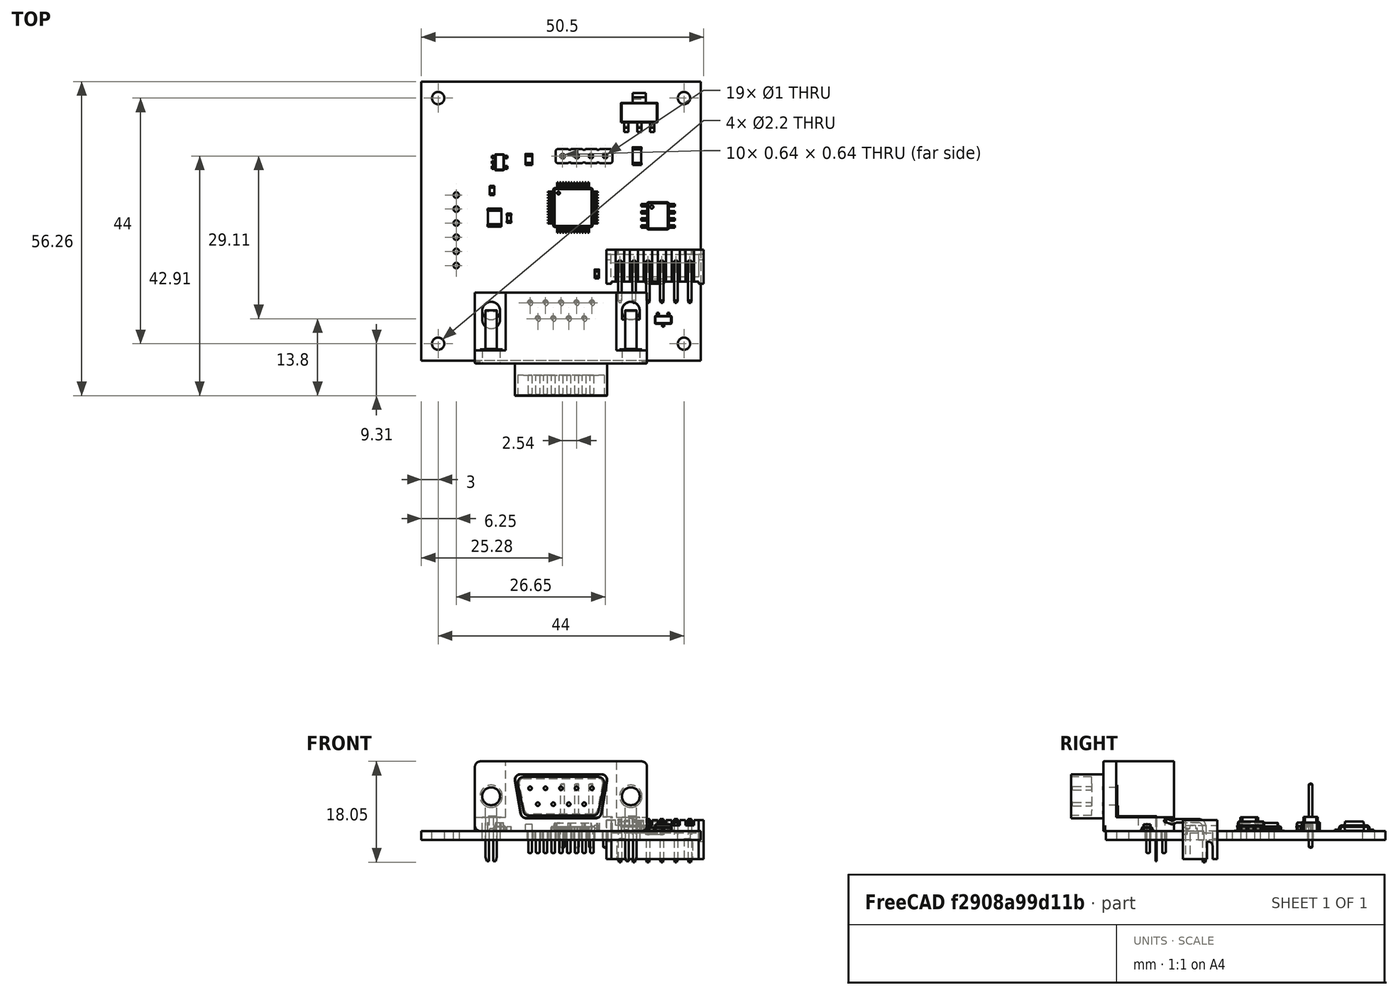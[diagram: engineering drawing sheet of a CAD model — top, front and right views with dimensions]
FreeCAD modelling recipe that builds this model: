
FCSTD DOCUMENT  (FreeCAD 0.21R33694 (Git))
Label: CTB-02_Assembled
License: All rights reserved
LicenseURL: http://en.wikipedia.org/wiki/All_rights_reserved
objects: App::Link×39, Part::Feature×34, App::Part×7, PartDesign::CoordinateSystem×1, Sketcher::SketchObject×1
note: 36 computed .brp shape members not serialized (recipe doc carries the construction recipe); baked Part::Feature solids carry a one-line shape summary decoded from their .brp

FEATURE [PartDesign::CoordinateSystem] Local_CS_1da8
  AttacherType = Attacher::AttachEngine3D
  MapMode = 2
  Support = -> [X_Axis001]
FEATURE [Part::Feature] Pcb_1da8
  Placement = pos=(-166.8,101.25,0) rot=(0,0,1;0rad)
  shape: bbox 50 x 50 x 1.6 mm, 31 faces (baked)
FEATURE [Sketcher::SketchObject] PCB_Sketch_1da8
  FullyConstrained = false
  sketch-geometry (4):
    g0: LineSegment StartX=-41.8 StartY=36.205 StartZ=0 EndX=8.2 EndY=36.205 EndZ=0
    g1: LineSegment StartX=8.2 StartY=36.205 StartZ=0 EndX=8.2 EndY=-13.795 EndZ=0
    g2: LineSegment StartX=8.2 StartY=-13.795 StartZ=0 EndX=-41.8 EndY=-13.795 EndZ=0
    g3: LineSegment StartX=-41.8 StartY=-13.795 StartZ=0 EndX=-41.8 EndY=36.205 EndZ=0
  constraints (4):
    c: Coincident(g2,g3)
    c: Coincident(g0,g3)
    c: Coincident(g1,g2)
    c: Coincident(g0,g1)
FEATURE [Part::Feature] Shape  label="R20_R_0603_1608Metric_5fb996311727"
  Placement = pos=(-29.15,16.7,0) rot=(0,0,1;1.5708rad)
  shape: bbox 0.8 x 1.6 x 0.45 mm, 26 faces (baked)
FEATURE [App::Link] R20_R_0603_1608Metric_5fb996311727_ln_  label="R8_R_0603_1608Metric_f8a9e1f5329c"
  LinkPlacement = pos=(1.6,-1.95,0) rot=(0,0,1;3.14159rad)
  LinkedObject = -> Shape
  Placement = pos=(1.6,-1.95,0) rot=(0,0,1;3.14159rad)
FEATURE [App::Link] R20_R_0603_1608Metric_5fb996311727_ln_001  label="R15_R_0603_1608Metric_9044ff0b4708"
  LinkPlacement = pos=(2.24952,17.675,0) rot=(0,0,-1;1.5708rad)
  LinkedObject = -> Shape
  Placement = pos=(2.24952,17.675,0) rot=(0,0,-1;1.5708rad)
FEATURE [App::Link] R20_R_0603_1608Metric_5fb996311727_ln_002  label="R2_R_0603_1608Metric_8a343aae5cf4"
  LinkPlacement = pos=(-31.05,26.5,0) rot=(0,0,-1;1.5708rad)
  LinkedObject = -> Shape
  Placement = pos=(-31.05,26.5,0) rot=(0,0,-1;1.5708rad)
FEATURE [App::Link] R20_R_0603_1608Metric_5fb996311727_ln_003  label="R14_R_0603_1608Metric_1eee93c9d580"
  LinkPlacement = pos=(4.24952,17.65,0) rot=(0,0,-1;1.5708rad)
  LinkedObject = -> Shape
  Placement = pos=(4.24952,17.65,0) rot=(0,0,-1;1.5708rad)
FEATURE [App::Link] R20_R_0603_1608Metric_5fb996311727_ln_004  label="R24_R_0603_1608Metric_4744c90dbd69"
  LinkPlacement = pos=(-28.8,6.7,0) rot=(0,0,1;0rad)
  LinkedObject = -> Shape
  Placement = pos=(-28.8,6.7,0) rot=(0,0,1;0rad)
FEATURE [App::Link] R20_R_0603_1608Metric_5fb996311727_ln_005  label="R9_R_0603_1608Metric_2fc7657f437f"
  LinkPlacement = pos=(-31.75,24.1,0) rot=(0,0,1;0rad)
  LinkedObject = -> Shape
  Placement = pos=(-31.75,24.1,0) rot=(0,0,1;0rad)
FEATURE [App::Link] R20_R_0603_1608Metric_5fb996311727_ln_006  label="R4_R_0603_1608Metric_9dc4eea49bad"
  LinkPlacement = pos=(-32.8,21.75,0) rot=(0,0,1;1.5708rad)
  LinkedObject = -> Shape
  Placement = pos=(-32.8,21.75,0) rot=(0,0,1;1.5708rad)
FEATURE [Part::Feature] Part__Feature  label="pin^SxB-XH-A-1(LF)(SN)_bent"
  shape: bbox 0.64 x 7.495 x 7.72 mm, 44 faces (baked)
FEATURE [Part::Feature] Part__Feature001  label="pin^SxB-XH-A-1(LF)(SN)"
  Placement = pos=(-2.5,2e-16,0) rot=(0,0,1;0rad)
  shape: bbox 0.64 x 7.495 x 7.72 mm, 22 faces (baked)
FEATURE [Part::Feature] Part__Feature002  label="pin^SxB-XH-A-1(LF)(SN)001"
  Placement = pos=(-5,5e-16,-1e-16) rot=(0,0,1;0rad)
  shape: bbox 0.64 x 7.495 x 7.72 mm, 22 faces (baked)
FEATURE [Part::Feature] Part__Feature003  label="pin^SxB-XH-A-1(LF)(SN)002"
  Placement = pos=(-7.5,7e-16,-1e-16) rot=(0,0,1;0rad)
  shape: bbox 0.64 x 7.495 x 7.72 mm, 22 faces (baked)
FEATURE [Part::Feature] Part__Feature004  label="pin^SxB-XH-A-1(LF)(SN)003"
  Placement = pos=(-10,1e-15,-1e-16) rot=(0,0,1;0rad)
  shape: bbox 0.64 x 7.495 x 7.72 mm, 22 faces (baked)
FEATURE [Part::Feature] Part__Feature005  label="pin^SxB-XH-A-1(LF)(SN)_bent001"
  Placement = pos=(-12.5,1.2e-15,-2e-16) rot=(0,0,1;0rad)
  shape: bbox 0.64 x 7.495 x 7.72 mm, 44 faces (baked)
FEATURE [Part::Feature] Part__Feature006  label="Body"
  Placement = pos=(6e-16,0,-5) rot=(0,1,0;3.14159rad)
  shape: bbox 17.4 x 6.1 x 7 mm, 94 faces (baked)
FEATURE [App::Part] S6B_XH_A_1  label="J2_S6B-XH-A-1_9f07903cdd4e"
  Group = -> [Part__Feature,Part__Feature001,Part__Feature002,Part__Feature003,Part__Feature004,Part__Feature005,Part__Feature006]
  Origin = -> Origin008
  Placement = pos=(-37.4,9.585,0) rot=(0.57735,0.57735,0.57735;2.0944rad)
FEATURE [App::Link] R20_R_0603_1608Metric_5fb996311727_ln_007  label="R30_R_0603_1608Metric_28c4134f9de7"
  LinkPlacement = pos=(-8.35,7.15,0) rot=(0,0,1;1.5708rad)
  LinkedObject = -> Shape
  Placement = pos=(-8.35,7.15,0) rot=(0,0,1;1.5708rad)
FEATURE [Part::Feature] Shape001  label="U3_SOT_223_728849c4b83c"
  Placement = pos=(-2.8,30.65,0) rot=(0,0,1;1.5708rad)
  shape: bbox 6.5 x 7 x 1.7 mm, 78 faces (baked)
FEATURE [App::Link] R20_R_0603_1608Metric_5fb996311727_ln_008  label="R12_R_0603_1608Metric_dfdb8e1241b6"
  LinkPlacement = pos=(-20.55,22,0) rot=(0,0,-1;1.5708rad)
  LinkedObject = -> Shape
  Placement = pos=(-20.55,22,0) rot=(0,0,-1;1.5708rad)
FEATURE [Part::Feature] Shape002  label="Q1_SOT_23_b1036018b4d2"
  Placement = pos=(1.5,-6.45,0) rot=(0,0,-1;1.5708rad)
  shape: bbox 3 x 2.5 x 1.2 mm, 76 faces (baked)
FEATURE [Part::Feature] Part__Feature007  label="CSTNE8M00GH5C000R0"
  shape: bbox 3 x 0.3 x 1.1 mm, 18 faces (baked)
FEATURE [Part::Feature] Part__Feature008  label="CSTNE8M00GH5C000R001"
  shape: bbox 0.2 x 0.5 x 1.3 mm, 6 faces (baked)
FEATURE [Part::Feature] Part__Feature009  label="CSTNE8M00GH5C000R002"
  shape: bbox 0.2 x 0.5 x 1.3 mm, 6 faces (baked)
FEATURE [Part::Feature] Part__Feature010  label="CSTNE8M00GH5C000R003"
  shape: bbox 0.4 x 0.5 x 1.3 mm, 6 faces (baked)
FEATURE [Part::Feature] Part__Feature011  label="CSTNE8M00GH5C000R004"
  shape: bbox 0.4 x 0.5 x 1.3 mm, 6 faces (baked)
FEATURE [Part::Feature] Part__Feature012  label="CSTNE8M00GH5C000R005"
  shape: bbox 0.4 x 0.45 x 1.3 mm, 6 faces (baked)
FEATURE [Part::Feature] Part__Feature013  label="CSTNE8M00GH5C000R006"
  shape: bbox 2 x 0.5 x 1.3 mm, 10 faces (baked)
FEATURE [App::Part] CSTNE8M00GH5C000R0  label="Y1_CSTNE8M00GH5C000R007_5459dfa8324f"
  Group = -> [Part__Feature007,Part__Feature008,Part__Feature009,Part__Feature010,Part__Feature011,Part__Feature012,Part__Feature013]
  Origin = -> Origin009
  Placement = pos=(-21.5,13.15,0) rot=(0.57735,-0.57735,-0.57735;2.0944rad)
FEATURE [Part::Feature] Shape003  label="C9_C_1206_3216Metric_4a6abfde341f"
  Placement = pos=(-3.2,22.85,0) rot=(0,0,1;1.5708rad)
  shape: bbox 1.6 x 3.2 x 1.6 mm, 28 faces (baked)
FEATURE [Part::Feature] Shape004  label="C13_C_0603_1608Metric_ec762f584ad8"
  Placement = pos=(-26.1,11.75,0) rot=(0,0,1;1.5708rad)
  shape: bbox 0.8 x 1.6 x 0.8 mm, 28 faces (baked)
FEATURE [Part::Feature] Shape005  label="D2_LED_0603_1608Metric_9a2b872fa988"
  Placement = pos=(-10.4,1.75,0) rot=(0,0,1;1.5708rad)
  shape: bbox 0.8 x 1.6 x 1.1 mm, 50 faces (baked)
FEATURE [App::Link] U3_SOT_223_728849c4b83c_ln_  label="U1_SOT_223_b2e5ecc5a7cd"
  LinkPlacement = pos=(-21.5,30.65,0) rot=(0,0,1;1.5708rad)
  LinkedObject = -> Shape001
  Placement = pos=(-21.5,30.65,0) rot=(0,0,1;1.5708rad)
FEATURE [App::Link] C13_C_0603_1608Metric_ec762f584ad8_ln_  label="C6_C_0603_1608Metric_85e27d3c77db"
  LinkPlacement = pos=(-27.7,24.7,0) rot=(0,0,1;3.14159rad)
  LinkedObject = -> Shape004
  Placement = pos=(-27.7,24.7,0) rot=(0,0,1;3.14159rad)
FEATURE [App::Link] C13_C_0603_1608Metric_ec762f584ad8_ln_001  label="C3_C_0603_1608Metric_23fe59c1562e"
  LinkPlacement = pos=(-31,21.75,0) rot=(0,0,1;1.5708rad)
  LinkedObject = -> Shape004
  Placement = pos=(-31,21.75,0) rot=(0,0,1;1.5708rad)
FEATURE [App::Link] R20_R_0603_1608Metric_5fb996311727_ln_009  label="R11_R_0603_1608Metric_7d51a89331da"
  LinkPlacement = pos=(-24.55,22,0) rot=(0,0,1;1.5708rad)
  LinkedObject = -> Shape
  Placement = pos=(-24.55,22,0) rot=(0,0,1;1.5708rad)
FEATURE [App::Link] R20_R_0603_1608Metric_5fb996311727_ln_010  label="R10_R_0603_1608Metric_22d4fa4ee4f3"
  LinkPlacement = pos=(-26.65,16.75,0) rot=(0,0,-1;1.5708rad)
  LinkedObject = -> Shape
  Placement = pos=(-26.65,16.75,0) rot=(0,0,-1;1.5708rad)
FEATURE [Part::Feature] Shape006  label="J3_PinHeader_1x04_P254mm_Vertical_68b31ef03787"
  Placement = pos=(-8.9,22.85,0) rot=(0,0,-1;1.5708rad)
  shape: bbox 10.16 x 2.54 x 11.54 mm, 100 faces (baked)
FEATURE [App::Link] R20_R_0603_1608Metric_5fb996311727_ln_011  label="R21_R_0603_1608Metric_610184494f20"
  LinkPlacement = pos=(-28.8,8.35,0) rot=(0,0,1;0rad)
  LinkedObject = -> Shape
  Placement = pos=(-28.8,8.35,0) rot=(0,0,1;0rad)
FEATURE [App::Link] R20_R_0603_1608Metric_5fb996311727_ln_012  label="R17_R_0603_1608Metric_b5563379a259"
  LinkPlacement = pos=(-19.1,1.725,0) rot=(0,0,1;1.5708rad)
  LinkedObject = -> Shape
  Placement = pos=(-19.1,1.725,0) rot=(0,0,1;1.5708rad)
FEATURE [App::Link] R20_R_0603_1608Metric_5fb996311727_ln_013  label="R18_R_0603_1608Metric_477e2f9ed346"
  LinkPlacement = pos=(-17.4,1.75,0) rot=(0,0,1;1.5708rad)
  LinkedObject = -> Shape
  Placement = pos=(-17.4,1.75,0) rot=(0,0,1;1.5708rad)
FEATURE [App::Link] R20_R_0603_1608Metric_5fb996311727_ln_014  label="R5_R_0603_1608Metric_079fbe4344ab"
  LinkPlacement = pos=(-15.6,1.75,0) rot=(0,0,1;1.5708rad)
  LinkedObject = -> Shape
  Placement = pos=(-15.6,1.75,0) rot=(0,0,1;1.5708rad)
FEATURE [App::Link] R20_R_0603_1608Metric_5fb996311727_ln_015  label="R3_R_0603_1608Metric_73b643512b8b"
  LinkPlacement = pos=(1.6,-3.65,0) rot=(0,0,1;0rad)
  LinkedObject = -> Shape
  Placement = pos=(1.6,-3.65,0) rot=(0,0,1;0rad)
FEATURE [Part::Feature] Shape007  label="U2_SOT_23_5_2c270eb65cb8"
  Placement = pos=(-27.8,21.75,0) rot=(0,0,1;0rad)
  shape: bbox 2.8 x 2.9 x 1.55 mm, 109 faces (baked)
FEATURE [Part::Feature] Shape008  label="C12_C_1210_3225Metric_a6954b44bc46"
  Placement = pos=(-28.7,11.85,0) rot=(0,0,1;1.5708rad)
  shape: bbox 2.5 x 3.2 x 2.5 mm, 28 faces (baked)
FEATURE [App::Link] R20_R_0603_1608Metric_5fb996311727_ln_016  label="R22_R_0603_1608Metric_aaec7f8dce7a"
  LinkPlacement = pos=(-28.8,5,0) rot=(0,0,1;0rad)
  LinkedObject = -> Shape
  Placement = pos=(-28.8,5,0) rot=(0,0,1;0rad)
FEATURE [Part::Feature] Shape009  label="C8_C_0805_2012Metric_1688cc946903"
  Placement = pos=(-22.55,22.25,0) rot=(0,0,1;1.5708rad)
  shape: bbox 1.25 x 2 x 1.25 mm, 28 faces (baked)
FEATURE [App::Link] Q1_SOT_23_b1036018b4d2_ln_  label="D1_SOT_23_b0d5b012e837"
  LinkPlacement = pos=(-11.9,28.25,0) rot=(0,0,1;0rad)
  LinkedObject = -> Shape002
  Placement = pos=(-11.9,28.25,0) rot=(0,0,1;0rad)
FEATURE [Part::Feature] Shape010  label="J1_DSUB-9_Male_Horizontal_P2.77x2.84mm_EdgePinOffset7.70mm_Housed_
MountingHolesOffset9.12mm_90076e21dd48"
  Placement = pos=(-22.35,-3.41967,0) rot=(0,0,1;0rad)
  shape: bbox 30.96 x 18.44 x 17.98 mm, 181 faces (baked)
FEATURE [App::Link] C13_C_0603_1608Metric_ec762f584ad8_ln_002  label="C19_C_0603_1608Metric_995048d5ef05"
  LinkPlacement = pos=(-21.55,16.9,0) rot=(0,0,1;3.14159rad)
  LinkedObject = -> Shape004
  Placement = pos=(-21.55,16.9,0) rot=(0,0,1;3.14159rad)
FEATURE [App::Link] R20_R_0603_1608Metric_5fb996311727_ln_017  label="R13_R_0603_1608Metric_37551f048aa7"
  LinkPlacement = pos=(-3.75048,17.75,0) rot=(0,0,-1;1.5708rad)
  LinkedObject = -> Shape
  Placement = pos=(-3.75048,17.75,0) rot=(0,0,-1;1.5708rad)
FEATURE [App::Link] C13_C_0603_1608Metric_ec762f584ad8_ln_003  label="C11_C_0603_1608Metric_e1d64a5043b0"
  LinkPlacement = pos=(5.14952,12.05,0) rot=(0,0,-1;1.5708rad)
  LinkedObject = -> Shape004
  Placement = pos=(5.14952,12.05,0) rot=(0,0,-1;1.5708rad)
FEATURE [App::Link] C8_C_0805_2012Metric_1688cc946903_ln_  label="C2_C_0805_2012Metric_3e8ded921b53"
  LinkPlacement = pos=(-27.05,31.75,0) rot=(0,0,-1;1.5708rad)
  LinkedObject = -> Shape009
  Placement = pos=(-27.05,31.75,0) rot=(0,0,-1;1.5708rad)
FEATURE [Part::Feature] Shape011  label="U4_SOIC_8_39x49mm_P127mm_61171556ec97"
  Placement = pos=(0.54952,12.15,0) rot=(0,0,1;0rad)
  shape: bbox 6 x 4.9 x 1.75 mm, 156 faces (baked)
FEATURE [App::Link] R20_R_0603_1608Metric_5fb996311727_ln_018  label="R1_R_0603_1608Metric_9b5c03b9db92"
  LinkPlacement = pos=(0.75,-9.25,0) rot=(0,0,1;3.14159rad)
  LinkedObject = -> Shape
  Placement = pos=(0.75,-9.25,0) rot=(0,0,1;3.14159rad)
FEATURE [App::Link] C13_C_0603_1608Metric_ec762f584ad8_ln_004  label="C14_C_0603_1608Metric_9308765661dd"
  LinkPlacement = pos=(-6.2,22.05,0) rot=(0,0,-1;1.5708rad)
  LinkedObject = -> Shape004
  Placement = pos=(-6.2,22.05,0) rot=(0,0,-1;1.5708rad)
FEATURE [App::Link] C9_C_1206_3216Metric_4a6abfde341f_ln_  label="C7_C_1206_3216Metric_b4d6b5bd6ad1"
  LinkPlacement = pos=(-8.3,28.25,0) rot=(0,0,-1;1.5708rad)
  LinkedObject = -> Shape003
  Placement = pos=(-8.3,28.25,0) rot=(0,0,-1;1.5708rad)
FEATURE [App::Link] C13_C_0603_1608Metric_ec762f584ad8_ln_005  label="C10_C_0603_1608Metric_30e2a4bc65d4"
  LinkPlacement = pos=(-0.9,23.45,0) rot=(0,0,1;1.5708rad)
  LinkedObject = -> Shape004
  Placement = pos=(-0.9,23.45,0) rot=(0,0,1;1.5708rad)
FEATURE [Part::Feature] Shape012  label="U5_LQFP_48_7x7mm_P05mm_9a45da788053"
  Placement = pos=(-14.67,13.65,0) rot=(0,0,1;0rad)
  shape: bbox 9 x 9 x 1.5 mm, 764 faces (baked)
FEATURE [App::Link] C9_C_1206_3216Metric_4a6abfde341f_ln_001  label="C4_C_1206_3216Metric_1186cc1c97c4"
  LinkPlacement = pos=(-15.6,28.55,0) rot=(0,0,-1;1.5708rad)
  LinkedObject = -> Shape003
  Placement = pos=(-15.6,28.55,0) rot=(0,0,-1;1.5708rad)
FEATURE [App::Link] C12_C_1210_3225Metric_a6954b44bc46_ln_  label="C1_C_1210_3225Metric_febb3d8b4366"
  LinkPlacement = pos=(-30.05,31.25,0) rot=(0,0,-1;1.5708rad)
  LinkedObject = -> Shape008
  Placement = pos=(-30.05,31.25,0) rot=(0,0,-1;1.5708rad)
FEATURE [App::Link] R20_R_0603_1608Metric_5fb996311727_ln_019  label="R6_R_0603_1608Metric_5a539fdbb717"
  LinkPlacement = pos=(-13.9,1.75,0) rot=(0,0,1;1.5708rad)
  LinkedObject = -> Shape
  Placement = pos=(-13.9,1.75,0) rot=(0,0,1;1.5708rad)
FEATURE [App::Link] R20_R_0603_1608Metric_5fb996311727_ln_020  label="R16_R_0603_1608Metric_a0c4ad1bf538"
  LinkPlacement = pos=(-20.8,1.7,0) rot=(0,0,-1;1.5708rad)
  LinkedObject = -> Shape
  Placement = pos=(-20.8,1.7,0) rot=(0,0,-1;1.5708rad)
FEATURE [App::Part] Top_1da8
  Group = -> [Shape,R20_R_0603_1608Metric_5fb996311727_ln_,R20_R_0603_1608Metric_5fb996311727_ln_001,R20_R_0603_1608Metric_5fb996311727_ln_002,R20_R_0603_1608Metric_5fb996311727_ln_003,R20_R_0603_1608Metric_5fb996311727_ln_004,R20_R_0603_1608Metric_5fb996311727_ln_005,R20_R_0603_1608Metric_5fb996311727_ln_006,S6B_XH_A_1,R20_R_0603_1608Metric_5fb996311727_ln_007,Shape001,+37 more]
  Origin = -> Origin003
FEATURE [App::Link] C13_C_0603_1608Metric_ec762f584ad8_ln_006  label="C17_C_0603_1608Metric_e6bd0ca13b07"
  LinkPlacement = pos=(-12.3,15.35,-1.6) rot=(0.707107,-0.707107,0;3.14159rad)
  LinkedObject = -> Shape004
  Placement = pos=(-12.3,15.35,-1.6) rot=(0.707107,-0.707107,0;3.14159rad)
FEATURE [App::Link] C13_C_0603_1608Metric_ec762f584ad8_ln_007  label="C16_C_0603_1608Metric_574b1417282d"
  LinkPlacement = pos=(-12.8,11.25,-1.6) rot=(0,1,0;3.14159rad)
  LinkedObject = -> Shape004
  Placement = pos=(-12.8,11.25,-1.6) rot=(0,1,0;3.14159rad)
FEATURE [App::Link] R20_R_0603_1608Metric_5fb996311727_ln_021  label="R26_R_0603_1608Metric_1764a2733b1e"
  LinkPlacement = pos=(-14.3,13,-1.6) rot=(1,0,0;3.14159rad)
  LinkedObject = -> Shape
  Placement = pos=(-14.3,13,-1.6) rot=(1,0,0;3.14159rad)
FEATURE [App::Link] C13_C_0603_1608Metric_ec762f584ad8_ln_008  label="C18_C_0603_1608Metric_81392f8e2ded"
  LinkPlacement = pos=(-17,15.25,-1.6) rot=(0.707107,-0.707107,0;3.14159rad)
  LinkedObject = -> Shape004
  Placement = pos=(-17,15.25,-1.6) rot=(0.707107,-0.707107,0;3.14159rad)
FEATURE [App::Link] R20_R_0603_1608Metric_5fb996311727_ln_022  label="R25_R_0603_1608Metric_aa714409e06c"
  LinkPlacement = pos=(-14.65,15.75,-1.6) rot=(0,1,0;3.14159rad)
  LinkedObject = -> Shape
  Placement = pos=(-14.65,15.75,-1.6) rot=(0,1,0;3.14159rad)
FEATURE [App::Link] C13_C_0603_1608Metric_ec762f584ad8_ln_009  label="C20_C_0603_1608Metric_0a61d1811865"
  LinkPlacement = pos=(-16.8,11.95,-1.6) rot=(0.707107,0.707107,0;3.14159rad)
  LinkedObject = -> Shape004
  Placement = pos=(-16.8,11.95,-1.6) rot=(0.707107,0.707107,0;3.14159rad)
FEATURE [App::Part] Bot_1da8
  Group = -> [C13_C_0603_1608Metric_ec762f584ad8_ln_006,C13_C_0603_1608Metric_ec762f584ad8_ln_007,R20_R_0603_1608Metric_5fb996311727_ln_021,C13_C_0603_1608Metric_ec762f584ad8_ln_008,R20_R_0603_1608Metric_5fb996311727_ln_022,C13_C_0603_1608Metric_ec762f584ad8_ln_009]
  Origin = -> Origin004
FEATURE [App::Part] Step_Models_1da8
  Group = -> [Top_1da8,Bot_1da8]
  Origin = -> Origin002
FEATURE [Part::Feature] Shape014  label="topTracks_1da8"
  Placement = pos=(-166.8,101.25,0.01) rot=(0,0,1;0rad)
  shape: bbox 47.58 x 40.55 x 0.0001 mm, 80 faces, 0 solids (baked)
FEATURE [Part::Feature] zones_area001  label="topZones_1da8"
  Placement = pos=(-166.8,101.25,0.01) rot=(0,0,1;0rad)
  shape: bbox 26.75 x 6.905 x 2e-07 mm, 2 faces, 0 solids (baked)
FEATURE [Part::Feature] topPads_1da8_  label="topPads_1da8_cut"
  Placement = pos=(0,0,0.02) rot=(0,0,1;0rad)
  shape: bbox 44.27 x 46.45 x 2e-07 mm, 234 faces, 0 solids (baked)
FEATURE [Part::Feature] pads_area003  label="botPads_1da8"
  Placement = pos=(-166.8,101.25,-1.62) rot=(0,0,1;0rad)
  shape: bbox 44.3 x 44.85 x 2e-07 mm, 107 faces, 0 solids (baked)
FEATURE [Part::Feature] Shape016  label="botTracks_1da8"
  Placement = pos=(-166.8,101.25,-1.61) rot=(0,0,1;0rad)
  shape: bbox 33.9 x 33.97 x 2e-07 mm, 16 faces, 0 solids (baked)
FEATURE [Part::Feature] zones_area003  label="botZones_1da8"
  Placement = pos=(-166.8,101.25,-1.61) rot=(0,0,1;0rad)
  shape: bbox 48.05 x 48.05 x 2e-07 mm, 1 faces, 0 solids (baked)
FEATURE [App::Part] Board_Geoms_1da8
  Group = -> [Pcb_1da8,PCB_Sketch_1da8,topPads_1da8_,Shape014,zones_area001,pads_area003,Shape016,zones_area003]
  Origin = -> Origin
FEATURE [App::Part] Board_1da8  label="CTB-01.kicad_pro"
  Group = -> [Local_CS_1da8,Board_Geoms_1da8,Step_Models_1da8]
  Origin = -> Origin001
